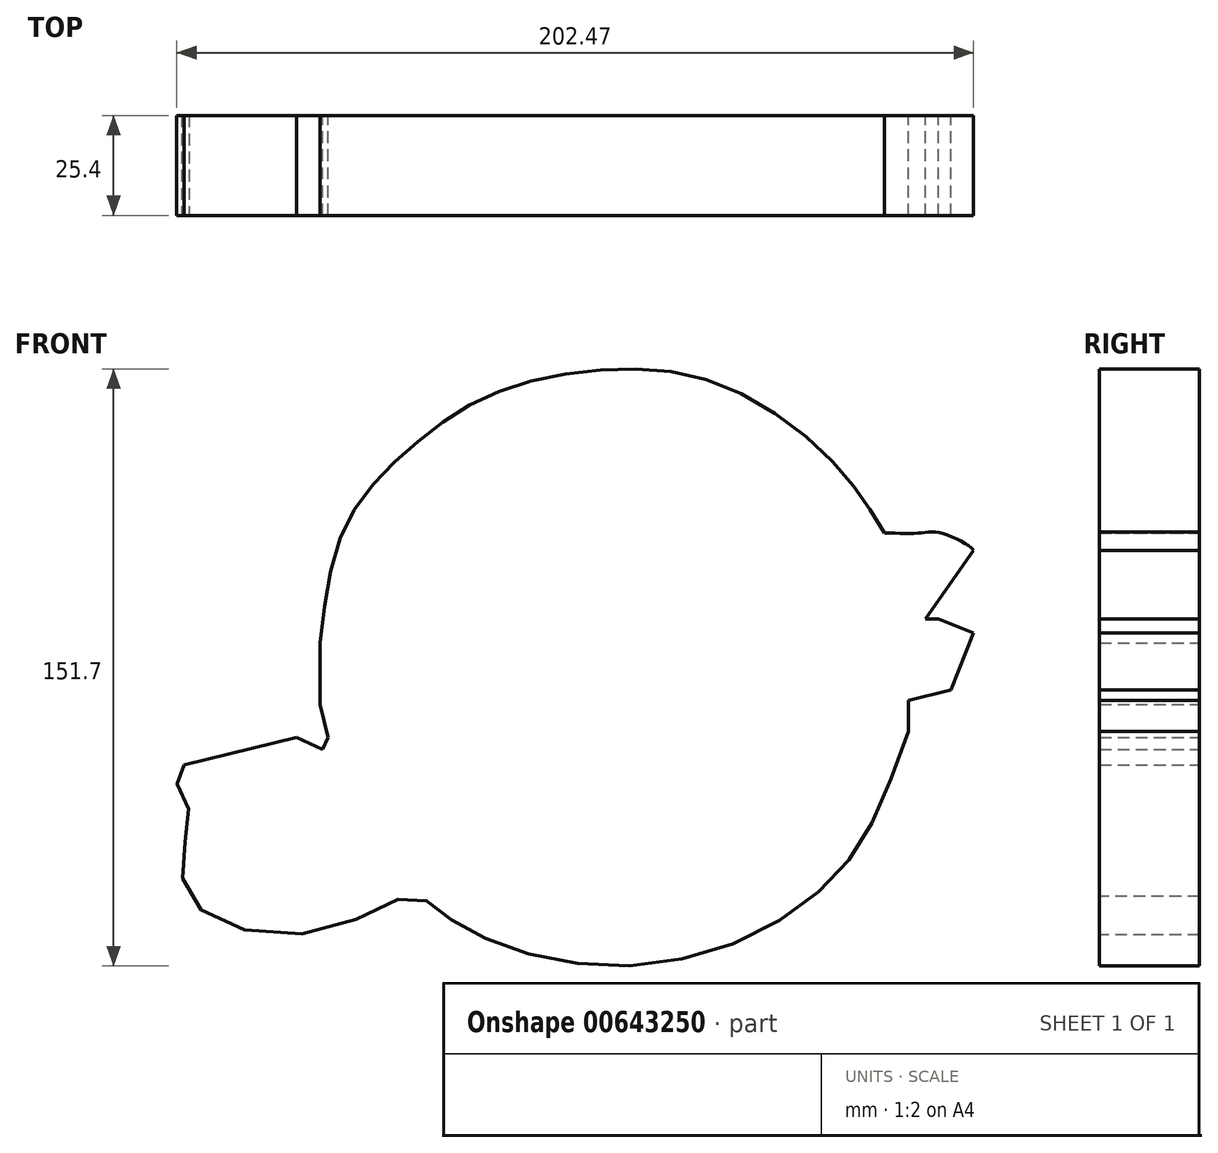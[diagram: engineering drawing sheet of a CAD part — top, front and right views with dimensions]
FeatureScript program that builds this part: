
annotation { "Feature Type Name" : "Feature", "Feature Type Description" : "" }
export const myFeature = defineFeature(function(context is Context, id is Id, definition is map)
    precondition{}
    {
        {
            var Q0;
            Q0=qCreatedBy(makeId("Front.planeOp"),FACE);
            var sketch = newSketch(context, id + "F0", { "sketchPlane" : qUnion([Q0])});
            skLineSegment(sketch, "E0", {"start": v(-62.11, -33.48) * mm, "end": v(-33.56, -26.5) * mm});
            skLineSegment(sketch, "E1", {"start": v(-33.56, -26.5) * mm, "end": v(-26.87, -29.53) * mm});
            skLineSegment(sketch, "E2", {"start": v(-26.87, -29.53) * mm, "end": v(-25.5, -26.5) * mm});
            skLineSegment(sketch, "E3", {"start": v(-25.5, -26.5) * mm, "end": v(-26.75, -21.36) * mm});
            skLineSegment(sketch, "E4", {"start": v(-26.75, -21.36) * mm, "end": v(-27.55, -18.08) * mm});
            skLineSegment(sketch, "E5", {"start": v(-27.55, -18.08) * mm, "end": v(-27.55, -11.6) * mm});
            skLineSegment(sketch, "E6", {"start": v(-27.55, -11.6) * mm, "end": v(-27.55, -2.49) * mm});
            skFitSpline(sketch, "E7", {"points": [v(-27.55, -2.49) * mm, v(-21.1, 27.27) * mm, v(-5.61, 46.1) * mm, v(14.74, 60.08) * mm, v(43.3, 66.76) * mm, v(74.28, 63.12) * mm, v(103.44, 42.77) * mm, v(115.9, 25.45) * mm], "startDerivative": vector(24.61, 214.18) * mm, "endDerivative": vector(82.17, -136) * mm});
            skFitSpline(sketch, "E8", {"points": [v(115.9, 25.45) * mm, v(125, 25.45) * mm, v(130.17, 25.45) * mm, v(137.77, 21.8) * mm, v(138.68, 20.6) * mm], "startDerivative": vector(31.27, -0.93) * mm, "endDerivative": vector(3.8, -8.3) * mm});
            skLineSegment(sketch, "E9", {"start": v(138.51, 20.95) * mm, "end": v(126.22, 3.58) * mm});
            skLineSegment(sketch, "E10", {"start": v(126.22, 3.58) * mm, "end": v(129.57, 3.58) * mm});
            skLineSegment(sketch, "E11", {"start": v(129.57, 3.58) * mm, "end": v(138.51, 0) * mm});
            skLineSegment(sketch, "E12", {"start": v(138.51, 0) * mm, "end": v(132.7, -14.5) * mm});
            skLineSegment(sketch, "E13", {"start": v(132.7, -14.5) * mm, "end": v(121.97, -17.08) * mm});
            skLineSegment(sketch, "E14", {"start": v(121.97, -17.08) * mm, "end": v(121.97, -24.97) * mm});
            skFitSpline(sketch, "E15", {"points": [v(121.97, -24.97) * mm, v(111.95, -49.58) * mm, v(98.89, -65.98) * mm, v(74.58, -79.96) * mm, v(44.2, -84.51) * mm, v(18.08, -79.04) * mm, v(3.5, -71.15) * mm, v(-4.1, -66.9) * mm, v(-25.66, -75.4) * mm, v(-56.64, -71.15) * mm, v(-62.72, -58.39) * mm, v(-60.9, -45.02) * mm, v(-63.93, -37.73) * mm, v(-62.11, -33.48) * mm], "startDerivative": vector(-99.7, -281.55) * mm, "endDerivative": vector(77.68, 104.96) * mm});
            skSolve(sketch);
        }
        {
            var Q0;
            Q0 = qSketchRegion(id + "F0", true);
            extrude(context, id + "F1", {"entities" : qUnion([Q0]), "depth" : 25.4 * mm, "offsetDistance" : 25.4 * mm});
        }
    });
